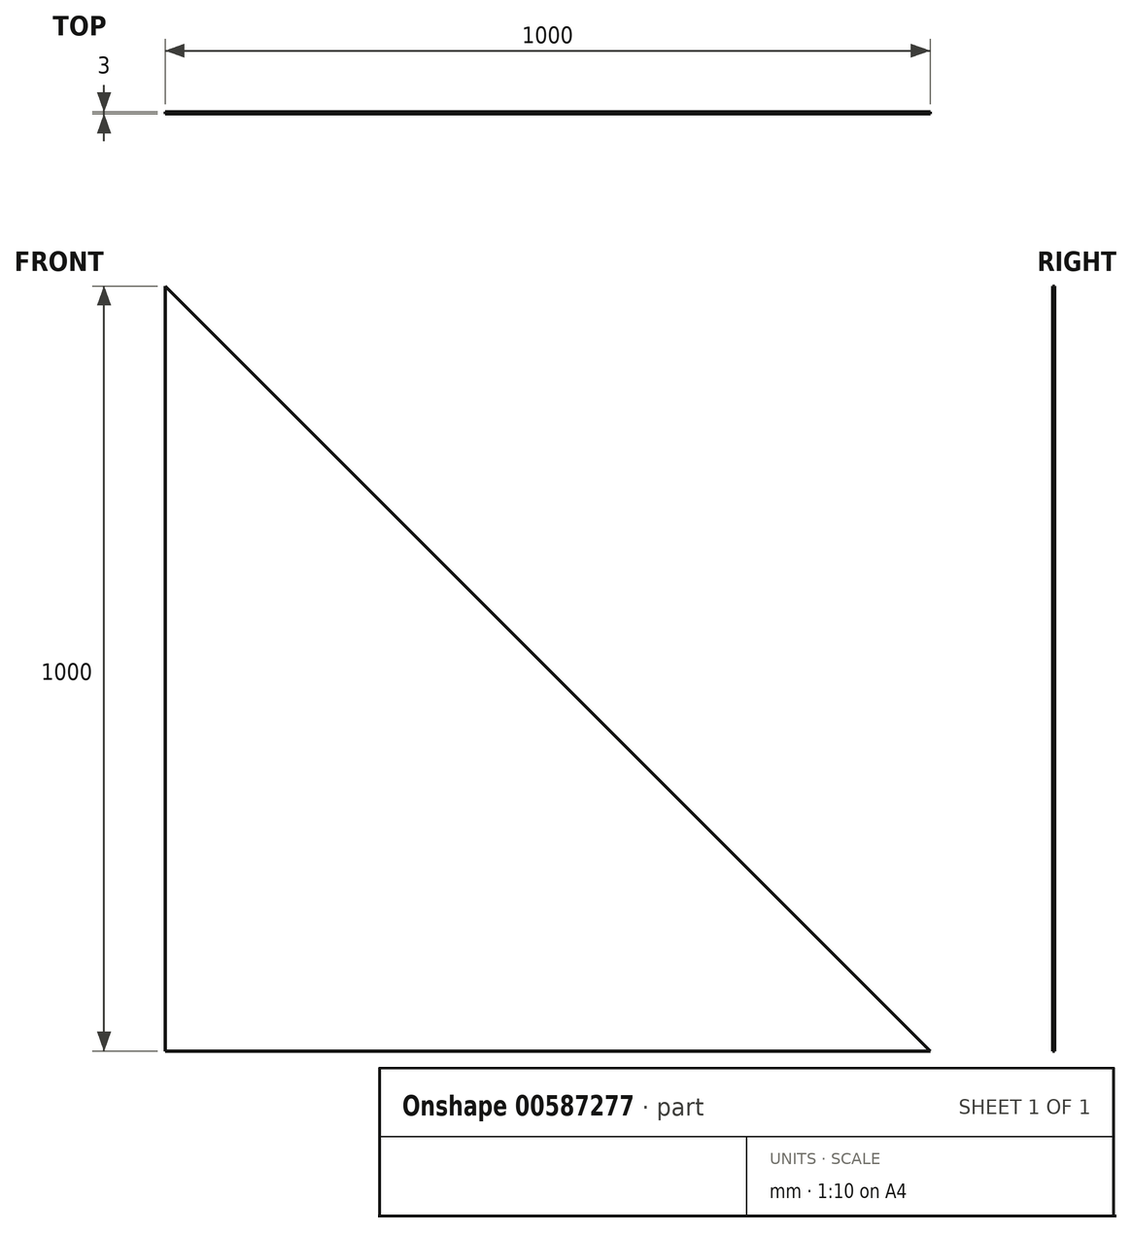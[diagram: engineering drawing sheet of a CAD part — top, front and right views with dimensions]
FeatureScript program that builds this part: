
annotation { "Feature Type Name" : "Feature", "Feature Type Description" : "" }
export const myFeature = defineFeature(function(context is Context, id is Id, definition is map)
    precondition{}
    {
        {
            var Q0;
            Q0=qCreatedBy(makeId("Front.planeOp"),FACE);
            var sketch = newSketch(context, id + "F0", { "sketchPlane" : qUnion([Q0])});
            skLineSegment(sketch, "E0", {"start": v(0, 0) * mm, "end": v(1000, 0) * mm});
            skLineSegment(sketch, "E1", {"start": v(1000, 0) * mm, "end": v(0, 1000) * mm});
            skLineSegment(sketch, "E2", {"start": v(0, 1000) * mm, "end": v(0, 0) * mm});
            skSolve(sketch);
        }
        {
            var Q0;
            Q0=makeQuery(id+"F0.imprint","IMPRINT",FACE,{"disambiguationData":[TD([[makeQuery(id+"F0.imprint","IMPRINT",EDGE,{"derivedFrom":sQuery(id+"F0.wireOp",EDGE,"E0")}),1.0]])]});
            extrude(context, id + "F1", {"entities" : qUnion([Q0]), "depth" : 3 * mm, "offsetDistance" : 25 * mm});
        }
    });
